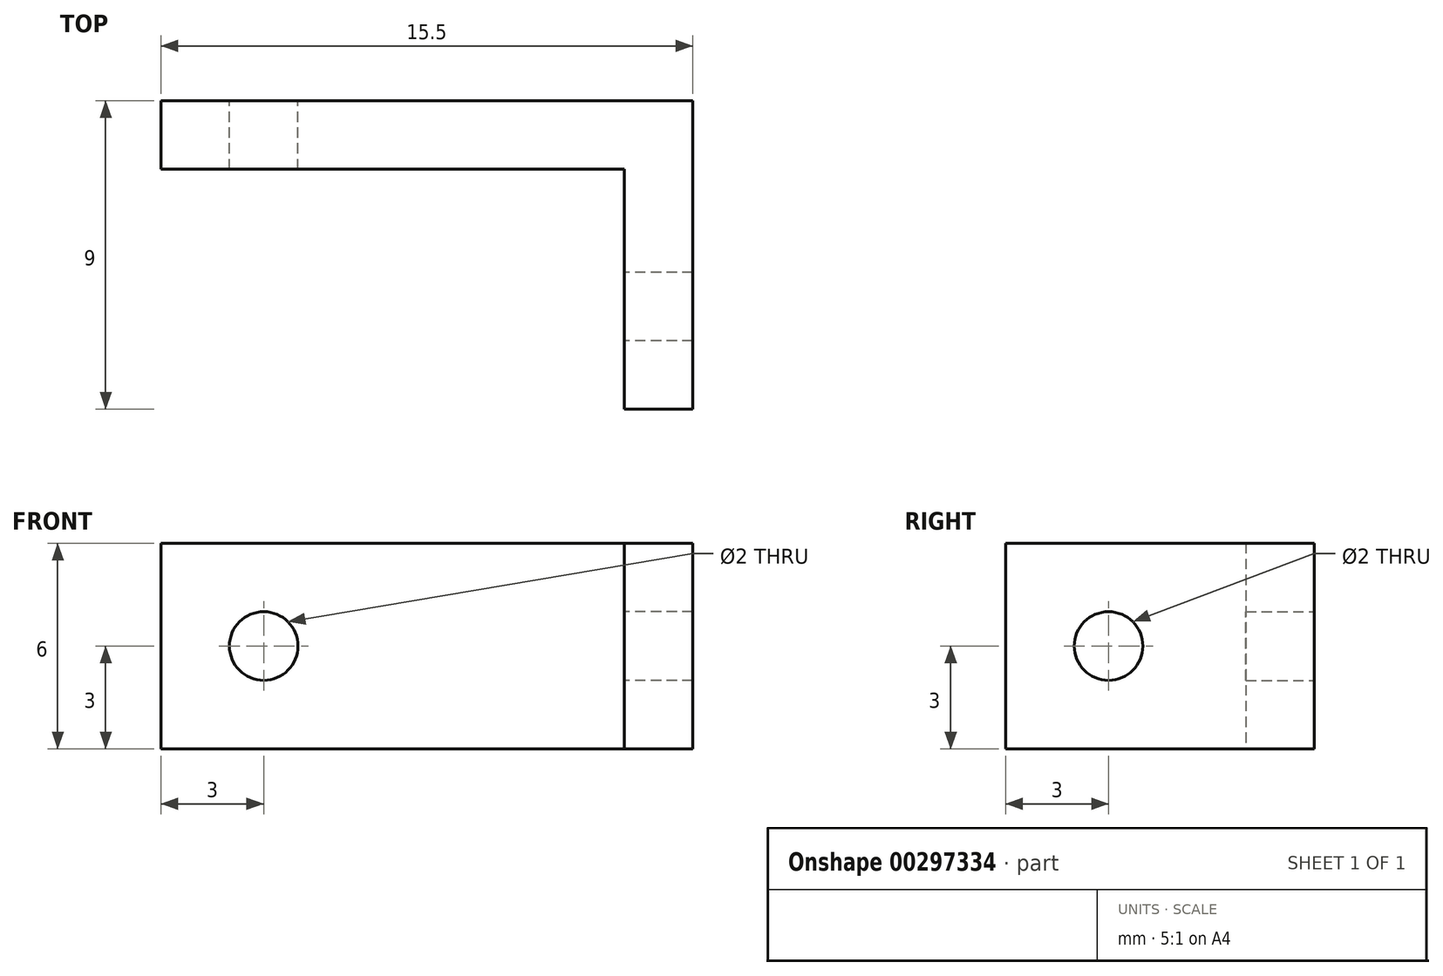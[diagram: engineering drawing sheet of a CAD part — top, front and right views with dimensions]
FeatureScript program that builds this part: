
annotation { "Feature Type Name" : "Feature", "Feature Type Description" : "" }
export const myFeature = defineFeature(function(context is Context, id is Id, definition is map)
    precondition{}
    {
        {
            var Q0;
            Q0=qCreatedBy(makeId("Front.planeOp"),FACE);
            var sketch = newSketch(context, id + "F0", { "sketchPlane" : qUnion([Q0])});
            skLineSegment(sketch, "E0.bottom", {"start": v(7.75, 3) * mm, "end": v(-7.75, 3) * mm});
            skLineSegment(sketch, "E0.top", {"start": v(7.75, -3) * mm, "end": v(-7.75, -3) * mm});
            skLineSegment(sketch, "E0.left", {"start": v(7.75, 3) * mm, "end": v(7.75, -3) * mm});
            skLineSegment(sketch, "E0.right", {"start": v(-7.75, 3) * mm, "end": v(-7.75, -3) * mm});
            skPoint(sketch, "E0.middle", {"position": v(0, 0) * mm});
            skCircle(sketch, "E1", {"center": v(-4.75, 0) * mm, "radius": 1 * mm});
            skSolve(sketch);
        }
        {
            var Q0;
            Q0 = qSketchRegion(id + "F0", true);
            extrude(context, id + "F1", {"entities" : qUnion([Q0]), "depth" : 2 * mm});
        }
        {
            var Q0;
            Q0=makeQuery(id+"F1.opExtrude","CAP_FACE",FACE,{"disambiguationData":[OSD([sQuery(id+"F0.wireOp",EDGE,"E0.bottom"),sQuery(id+"F0.wireOp",EDGE,"E0.top"),sQuery(id+"F0.wireOp",EDGE,"E0.left"),sQuery(id+"F0.wireOp",EDGE,"E0.right"),sQuery(id+"F0.wireOp",EDGE,"E1")])],"isStart":false});
            var sketch = newSketch(context, id + "F2", { "sketchPlane" : qUnion([Q0])});
            skLineSegment(sketch, "E2.bottom", {"start": v(7.75, 3) * mm, "end": v(5.75, 3) * mm});
            skLineSegment(sketch, "E2.top", {"start": v(7.75, -3) * mm, "end": v(5.75, -3) * mm});
            skLineSegment(sketch, "E2.left", {"start": v(7.75, 3) * mm, "end": v(7.75, -3) * mm});
            skLineSegment(sketch, "E2.right", {"start": v(5.75, 3) * mm, "end": v(5.75, -3) * mm});
            skSolve(sketch);
        }
        {
            var Q0;
            Q0 = qSketchRegion(id + "F2", true);
            extrude(context, id + "F3", {"entities" : qUnion([Q0]), "operationType" : NewBodyOperationType.ADD, "depth" : 7 * mm});
        }
        {
            var Q0;
            Q0=makeQuery(id+"F3.opExtrude","SWEPT_FACE",FACE,{"disambiguationData":[OSD([sQuery(id+"F2.wireOp",EDGE,"E2.right")])]});
            var sketch = newSketch(context, id + "F4", { "sketchPlane" : qUnion([Q0])});
            skCircle(sketch, "E3", {"center": v(6, 0) * mm, "radius": 1 * mm});
            skSolve(sketch);
        }
        {
            var Q0;
            Q0 = qSketchRegion(id + "F4", true);
            extrude(context, id + "F5", {"entities" : qUnion([Q0]), "operationType" : NewBodyOperationType.REMOVE, "oppositeDirection" : true, "depth" : 25 * mm});
        }
    });
